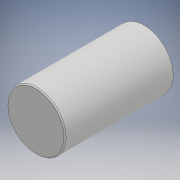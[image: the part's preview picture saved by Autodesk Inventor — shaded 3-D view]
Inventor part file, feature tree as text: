
AUTODESK INVENTOR PART (.ipt)
format: ipt  version: 2018 (Build 220112000, 112)  size: 267,264 bytes
history: native  units: mm
features: extrude x4, fillet x4, sketch x4
ambient origin geometry x8: Origin, YZ Plane, XZ Plane, XY Plane, X Axis, Y Axis, Z Axis, Center Point
bodies: Solid1 (feature_tree)
feature tree (12):
  extrude  "Extrusion1"  Depth=48.0mm
  extrude  "Extrusion2"  Depth=1.0mm TaperAngle=0.0deg
  fillet  "Fillet1"  Radius=3.0mm
  fillet  "Fillet2"  Radius=1.0mm
  extrude  "Extrusion3"  Depth=2.0mm
  fillet  "Fillet3"  Radius=40.0mm
  fillet  "Fillet4"  Radius=92.0mm
  extrude  "Extrusion4"  Depth=1.0mm
  sketch  "Sketch1"  dims[d0=50.0mm d1=48.0mm]
  sketch  "Sketch2"  dims[d2=90.0mm d3=0.0mm d4=3.0mm d5=0.0mm d6=3.0mm d7=1.0mm]
  sketch  "Sketch3"  dims[d8=5.0mm d9=2.0mm d10=40.0mm d12=360.0deg d14=92.0mm d15=0.0mm]
  sketch  "Sketch4"  dims[d16=1.0mm d17=1.0mm d18=5.0mm d19=0.0mm]
